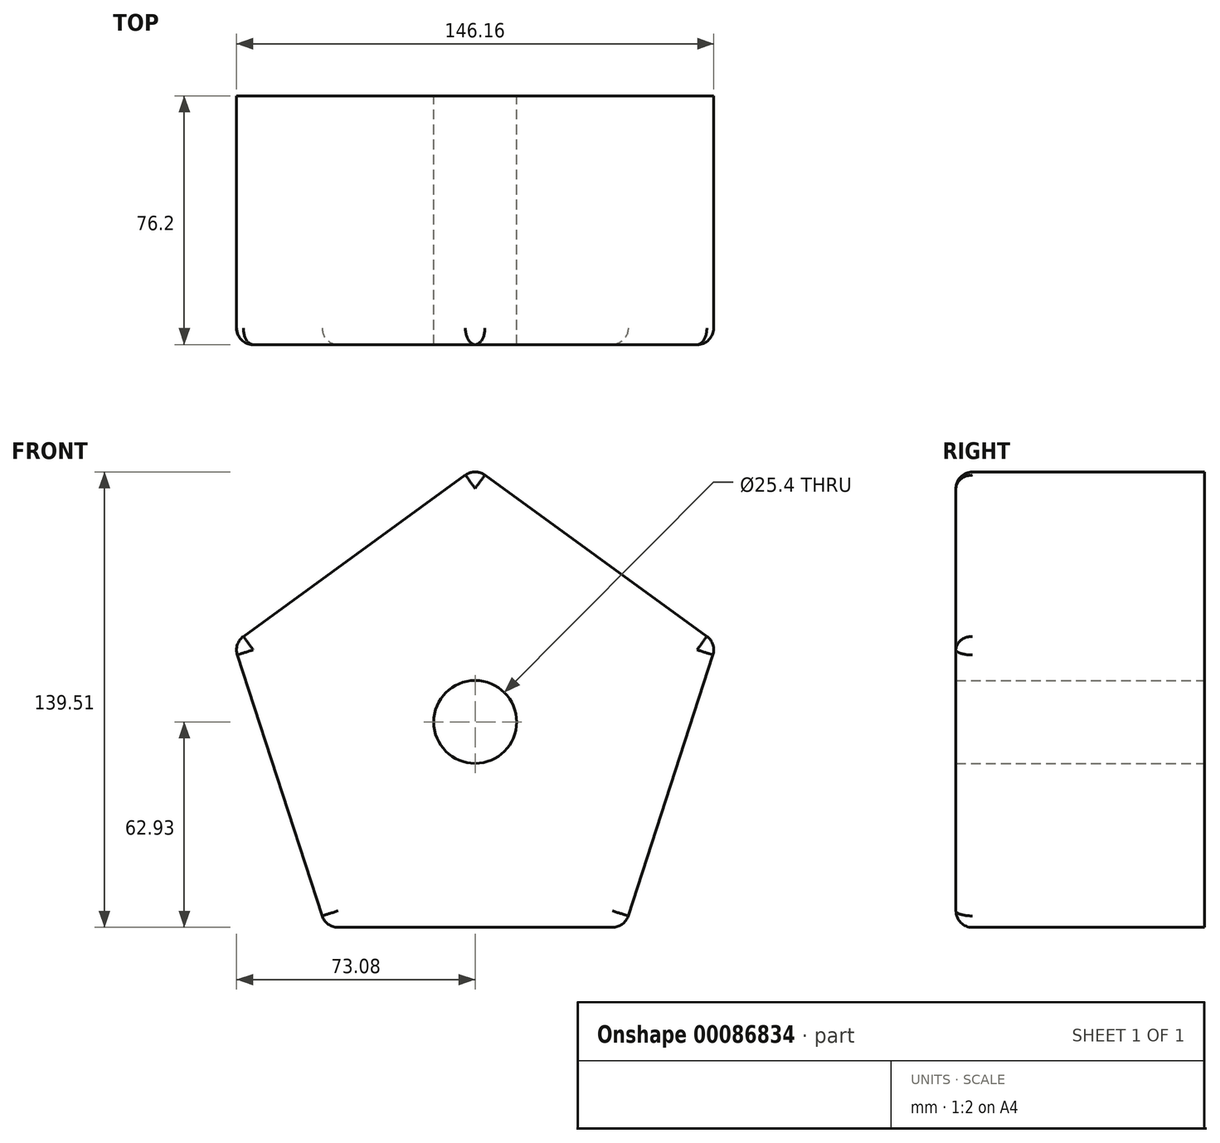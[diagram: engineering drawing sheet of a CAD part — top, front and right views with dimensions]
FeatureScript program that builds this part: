
annotation { "Feature Type Name" : "Feature", "Feature Type Description" : "" }
export const myFeature = defineFeature(function(context is Context, id is Id, definition is map)
    precondition{}
    {
        {
            var Q0;
            Q0=qCreatedBy(makeId("Front.planeOp"),FACE);
            var sketch = newSketch(context, id + "F0", { "sketchPlane" : qUnion([Q0])});
            skCircle(sketch, "E0.cCircle", {"center": v(-76.2, -76.2) * mm, "radius": 62.93 * mm, "construction": true});
            skLineSegment(sketch, "E0.0", {"start": v(-2.22, -52.16) * mm, "end": v(-30.48, -139.13) * mm});
            skLineSegment(sketch, "E0.1", {"start": v(-30.48, -139.13) * mm, "end": v(-121.92, -139.13) * mm});
            skLineSegment(sketch, "E0.2", {"start": v(-121.92, -139.13) * mm, "end": v(-150.18, -52.16) * mm});
            skLineSegment(sketch, "E0.3", {"start": v(-150.18, -52.16) * mm, "end": v(-76.2, 1.58) * mm});
            skLineSegment(sketch, "E0.4", {"start": v(-76.2, 1.58) * mm, "end": v(-2.22, -52.16) * mm});
            skPoint(sketch, "E0.0.midPoint", {"position": v(-16.35, -95.65) * mm});
            skSolve(sketch);
        }
        {
            var Q0;
            Q0=makeQuery(id+"F0.imprint","IMPRINT",FACE,{"disambiguationData":[TD([[makeQuery(id+"F0.imprint","IMPRINT",EDGE,{"derivedFrom":sQuery(id+"F0.wireOp",EDGE,"E0.0")}),-1.0]])]});
            extrude(context, id + "F1", {"entities" : qUnion([Q0]), "depth" : 76.2 * mm});
        }
        {
            var Q0;
            Q0=makeQuery(id+"F1.opExtrude","CAP_FACE",FACE,{"disambiguationData":[OSD([sQuery(id+"F0.wireOp",EDGE,"E0.0"),sQuery(id+"F0.wireOp",EDGE,"E0.1"),sQuery(id+"F0.wireOp",EDGE,"E0.2"),sQuery(id+"F0.wireOp",EDGE,"E0.3"),sQuery(id+"F0.wireOp",EDGE,"E0.4")])],"isStart":false});
            fillet(context, id + "F2", {"entities" : qUnion([Q0]), "radius" : 5.08 * mm, "tangentPropagation" : true, "allowEdgeOverflow" : false});
        }
        {
            var Q0;
            Q0=makeQuery(id+"F2.opFillet","BLEND_EDGE",EDGE,{"blendedFrom":[makeQuery(id+"F1.opExtrude","CAP_EDGE",EDGE,{"disambiguationData":[OSD([sQuery(id+"F0.wireOp",EDGE,"E0.2")])],"isStart":false}),makeQuery(id+"F1.opExtrude","CAP_EDGE",EDGE,{"disambiguationData":[OSD([sQuery(id+"F0.wireOp",EDGE,"E0.3")])],"isStart":false})],"blendedInto":[]});
            fillet(context, id + "F3", {"entities" : qUnion([Q0]), "radius" : 5.08 * mm, "tangentPropagation" : true, "allowEdgeOverflow" : false});
        }
        {
            var Q0;
            Q0=makeQuery(id+"F1.opExtrude","SWEPT_EDGE",EDGE,{"disambiguationData":[OSD([sQuery(id+"F0.wireOp",EDGE,"E0.1"),sQuery(id+"F0.wireOp",EDGE,"E0.2")])]});
            fillet(context, id + "F4", {"entities" : qUnion([Q0]), "radius" : 5.08 * mm, "tangentPropagation" : true, "allowEdgeOverflow" : false});
        }
        {
            var Q0;
            Q0=makeQuery(id+"F1.opExtrude","SWEPT_EDGE",EDGE,{"disambiguationData":[OSD([sQuery(id+"F0.wireOp",EDGE,"E0.0"),sQuery(id+"F0.wireOp",EDGE,"E0.1")])]});
            var Q1;
            Q1=makeQuery(id+"F1.opExtrude","SWEPT_EDGE",EDGE,{"disambiguationData":[OSD([sQuery(id+"F0.wireOp",EDGE,"E0.0"),sQuery(id+"F0.wireOp",EDGE,"E0.4")])]});
            fillet(context, id + "F5", {"entities" : qUnion([Q0, Q1]), "radius" : 5.08 * mm, "tangentPropagation" : true, "allowEdgeOverflow" : false});
        }
        {
            var Q0;
            Q0=makeQuery(id+"F1.opExtrude","SWEPT_EDGE",EDGE,{"disambiguationData":[OSD([sQuery(id+"F0.wireOp",EDGE,"E0.3"),sQuery(id+"F0.wireOp",EDGE,"E0.4")])]});
            fillet(context, id + "F6", {"entities" : qUnion([Q0]), "radius" : 5.08 * mm, "tangentPropagation" : true, "allowEdgeOverflow" : false});
        }
        {
            var Q0;
            Q0=sQuery(id+"F0.wireOp",VERTEX,"E0.cCircle.center");
            var Q1;
            Q1=makeQuery(id+"F1.opExtrude","SWEPT_BODY",BODY,{"disambiguationData":[OSD([sQuery(id+"F0.wireOp",EDGE,"E0.0"),sQuery(id+"F0.wireOp",EDGE,"E0.1"),sQuery(id+"F0.wireOp",EDGE,"E0.2"),sQuery(id+"F0.wireOp",EDGE,"E0.3"),sQuery(id+"F0.wireOp",EDGE,"E0.4")])]});
            hole(context, id + "F7", {"style" : HoleStyle.SIMPLE, "endStyle" : HoleEndStyle.THROUGH, "oppositeDirection" : true, "holeDiameter" : 25.4 * mm, "locations" : qUnion([Q0]), "scope" : qUnion([Q1]), "isTappedThrough" : true});
        }
    });
